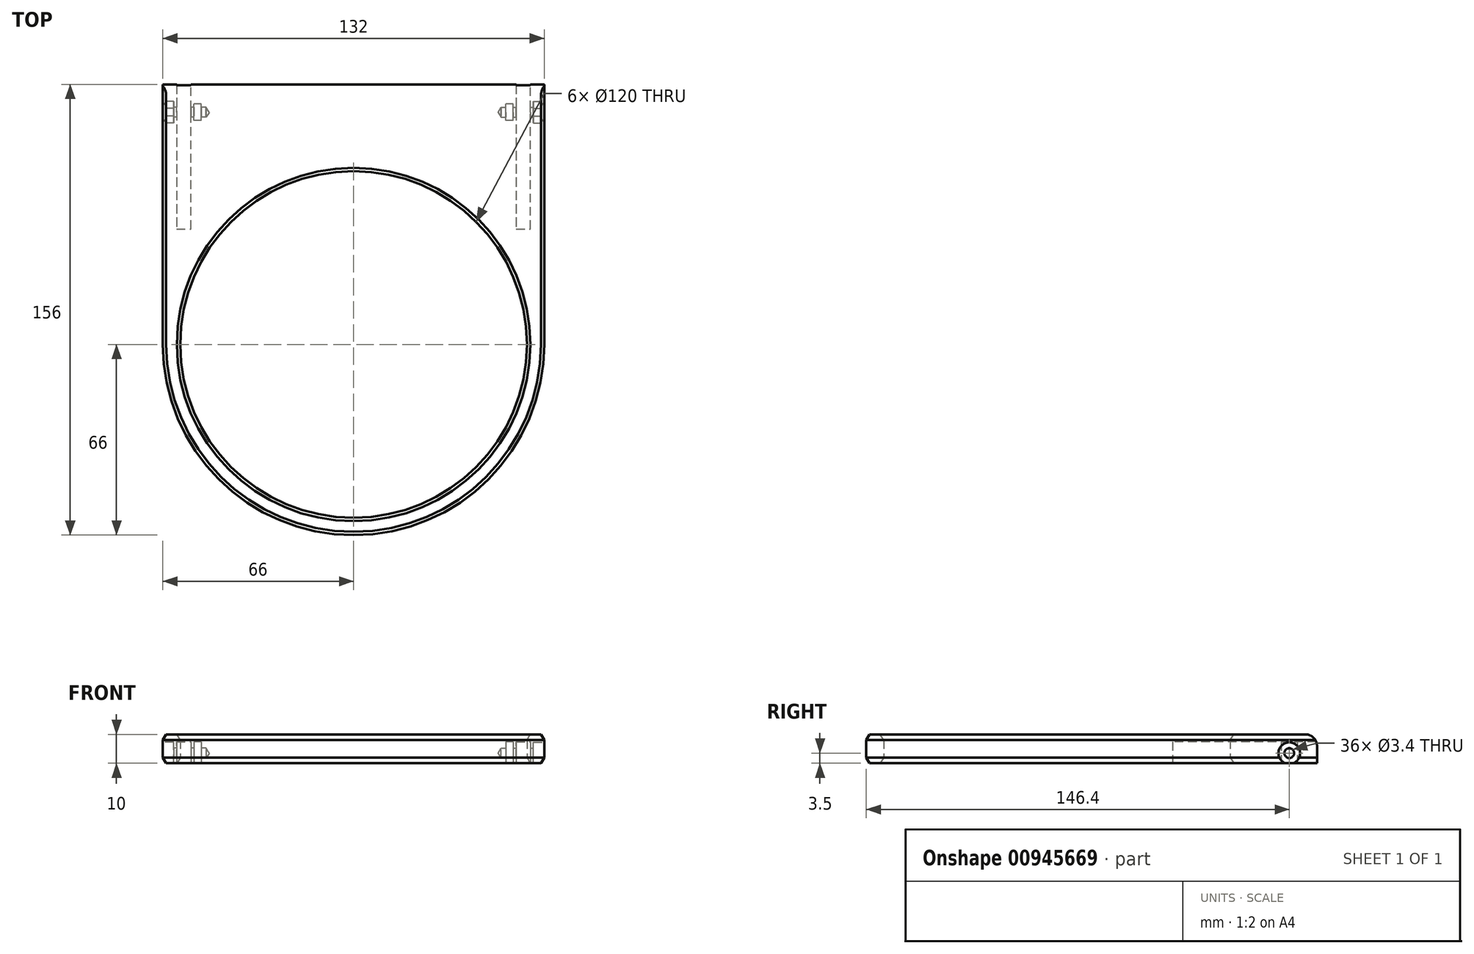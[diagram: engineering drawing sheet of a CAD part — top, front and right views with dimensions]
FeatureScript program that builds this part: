
annotation { "Feature Type Name" : "Feature", "Feature Type Description" : "" }
export const myFeature = defineFeature(function(context is Context, id is Id, definition is map)
    precondition{}
    {
        {
            var Q0;
            Q0=qCreatedBy(makeId("Top.planeOp"),FACE);
            var sketch = newSketch(context, id + "F0", { "sketchPlane" : qUnion([Q0])});
            skArc(sketch, "E0", {"start": v(-66, 0) * mm, "mid": v(0, -66) * mm, "end": v(66, 0) * mm});
            skLineSegment(sketch, "E1", {"start": v(-66, 0) * mm, "end": v(-66, 90) * mm});
            skLineSegment(sketch, "E2", {"start": v(-66, 90) * mm, "end": v(66, 90) * mm});
            skLineSegment(sketch, "E3", {"start": v(66, 90) * mm, "end": v(66, 0) * mm});
            skCircle(sketch, "E4", {"center": v(0, 0) * mm, "radius": 60 * mm});
            skSolve(sketch);
        }
        {
            var Q0;
            Q0=makeQuery(id+"F0.imprint","IMPRINT",FACE,{"disambiguationData":[TD([[makeQuery(id+"F0.imprint","IMPRINT",EDGE,{"derivedFrom":sQuery(id+"F0.wireOp",EDGE,"E0")}),1.0]])]});
            extrude(context, id + "F1", {"entities" : qUnion([Q0]), "depth" : 10 * mm, "offsetDistance" : 25 * mm});
        }
        {
            var Q0;
            Q0=makeQuery(id+"F1.opExtrude","CAP_EDGE",EDGE,{"disambiguationData":[OSD([sQuery(id+"F0.wireOp",EDGE,"E0")])],"isStart":true});
            var Q1;
            Q1=makeQuery(id+"F1.opExtrude","CAP_EDGE",EDGE,{"disambiguationData":[OSD([sQuery(id+"F0.wireOp",EDGE,"E0")])],"isStart":false});
            var Q2;
            Q2=makeQuery(id+"F1.opExtrude","CAP_EDGE",EDGE,{"disambiguationData":[OSD([sQuery(id+"F0.wireOp",EDGE,"E4")])],"isStart":false});
            var Q3;
            Q3=makeQuery(id+"F1.opExtrude","CAP_EDGE",EDGE,{"disambiguationData":[OSD([sQuery(id+"F0.wireOp",EDGE,"E4")])],"isStart":true});
            chamfer(context, id + "F2", {"entities" : qUnion([Q0, Q1, Q2, Q3]), "chamferType" : ChamferType.OFFSET_ANGLE, "width" : 2 * mm, "oppositeDirection" : false, "angle" : 30 * degree, "tangentPropagation" : true});
        }
        {
            var Q0;
            Q0=makeQuery(id+"F1.opExtrude","CAP_EDGE",EDGE,{"disambiguationData":[OSD([sQuery(id+"F0.wireOp",EDGE,"E2")])],"isStart":false});
            fillet(context, id + "F3", {"entities" : qUnion([Q0]), "radius" : 4 * mm, "tangentPropagation" : true, "allowEdgeOverflow" : false});
        }
        {
            var Q0;
            Q0=makeQuery(id+"F1.opExtrude","CAP_FACE",FACE,{"disambiguationData":[OSD([sQuery(id+"F0.wireOp",EDGE,"E0"),sQuery(id+"F0.wireOp",EDGE,"E1"),sQuery(id+"F0.wireOp",EDGE,"E2"),sQuery(id+"F0.wireOp",EDGE,"E3"),sQuery(id+"F0.wireOp",EDGE,"E4")])],"isStart":true});
            var sketch = newSketch(context, id + "F4", { "sketchPlane" : qUnion([Q0])});
            skLineSegment(sketch, "E5", {"start": v(-61.25, -90) * mm, "end": v(-61.25, -40) * mm});
            skLineSegment(sketch, "E6", {"start": v(-61.25, -40) * mm, "end": v(-56.25, -40) * mm});
            skLineSegment(sketch, "E7", {"start": v(-56.25, -40) * mm, "end": v(-56.25, -90) * mm});
            skLineSegment(sketch, "E8", {"start": v(56.25, -90) * mm, "end": v(56.25, -40) * mm});
            skLineSegment(sketch, "E9", {"start": v(56.25, -40) * mm, "end": v(61.25, -40) * mm});
            skLineSegment(sketch, "E10", {"start": v(61.25, -40) * mm, "end": v(61.25, -90) * mm});
            skLineSegment(sketch, "E11.bottom", {"start": v(-52.65, -77.55) * mm, "end": v(-55.25, -77.55) * mm});
            skLineSegment(sketch, "E11.top", {"start": v(-52.65, -83.25) * mm, "end": v(-55.25, -83.25) * mm});
            skLineSegment(sketch, "E11.left", {"start": v(-52.65, -77.55) * mm, "end": v(-52.65, -83.25) * mm});
            skLineSegment(sketch, "E11.right", {"start": v(-55.25, -77.55) * mm, "end": v(-55.25, -83.25) * mm});
            skPoint(sketch, "E11.middle", {"position": v(-53.95, -80.4) * mm});
            skLineSegment(sketch, "E12.bottom", {"start": v(55.25, -77.55) * mm, "end": v(52.65, -77.55) * mm});
            skLineSegment(sketch, "E12.top", {"start": v(55.25, -83.25) * mm, "end": v(52.65, -83.25) * mm});
            skLineSegment(sketch, "E12.left", {"start": v(55.25, -77.55) * mm, "end": v(55.25, -83.25) * mm});
            skLineSegment(sketch, "E12.right", {"start": v(52.65, -77.55) * mm, "end": v(52.65, -83.25) * mm});
            skPoint(sketch, "E12.middle", {"position": v(53.95, -80.4) * mm});
            skSolve(sketch);
        }
        {
            var Q0;
            {var subQ0=sQuery(id+"F4.wireOp",EDGE,"E8");Q0=makeQuery(id+"F4.imprint","IMPRINT",FACE,{"disambiguationData":[TD([[makeQuery(id+"F4.imprint","IMPRINT",EDGE,{"derivedFrom":subQ0}),-1.0]])]});}
            var Q1;
            {var subQ0=sQuery(id+"F4.wireOp",EDGE,"E5");Q1=makeQuery(id+"F4.imprint","IMPRINT",FACE,{"disambiguationData":[TD([[makeQuery(id+"F4.imprint","IMPRINT",EDGE,{"derivedFrom":subQ0}),-1.0]])]});}
            var Q2;
            Q2=makeQuery(id+"F4.imprint","IMPRINT",FACE,{"disambiguationData":[TD([[makeQuery(id+"F4.imprint","IMPRINT",EDGE,{"derivedFrom":sQuery(id+"F4.wireOp",EDGE,"E11.bottom")}),1.0]])]});
            var Q3;
            Q3=makeQuery(id+"F4.imprint","IMPRINT",FACE,{"disambiguationData":[TD([[makeQuery(id+"F4.imprint","IMPRINT",EDGE,{"derivedFrom":sQuery(id+"F4.wireOp",EDGE,"E12.bottom")}),1.0]])]});
            extrude(context, id + "F5", {"entities" : qUnion([Q0, Q1, Q2, Q3]), "operationType" : NewBodyOperationType.REMOVE, "oppositeDirection" : true, "depth" : 7.4 * mm, "offsetDistance" : 25 * mm});
        }
        {
            var Q0;
            Q0=makeQuery(id+"F1.opExtrude","SWEPT_FACE",FACE,{"disambiguationData":[OSD([sQuery(id+"F0.wireOp",EDGE,"E1")])]});
            var sketch = newSketch(context, id + "F6", { "sketchPlane" : qUnion([Q0])});
            skPoint(sketch, "E13", {"position": v(-80.4, 3.5) * mm});
            skSolve(sketch);
        }
        {
            var Q0;
            Q0=makeQuery(id+"F1.opExtrude","SWEPT_FACE",FACE,{"disambiguationData":[OSD([sQuery(id+"F0.wireOp",EDGE,"E3")])]});
            var sketch = newSketch(context, id + "F7", { "sketchPlane" : qUnion([Q0])});
            skPoint(sketch, "E14", {"position": v(80.4, 3.5) * mm});
            skSolve(sketch);
        }
        {
            var Q0;
            Q0=sQuery(id+"F6.wireOp",VERTEX,"E13");
            var Q1;
            Q1=sQuery(id+"F7.wireOp",VERTEX,"E14");
            var Q2;
            Q2=makeQuery(id+"F1.opExtrude","SWEPT_BODY",BODY,{"disambiguationData":[OSD([sQuery(id+"F0.wireOp",EDGE,"E0"),sQuery(id+"F0.wireOp",EDGE,"E1"),sQuery(id+"F0.wireOp",EDGE,"E2"),sQuery(id+"F0.wireOp",EDGE,"E3"),sQuery(id+"F0.wireOp",EDGE,"E4")])]});
            hole(context, id + "F8", {"style" : HoleStyle.C_BORE, "endStyle" : HoleEndStyle.BLIND, "holeDiameter" : 3.4 * mm, "cBoreDiameter" : 7.5 * mm, "cBoreDepth" : 3.75 * mm, "majorDiameter" : 5 * mm, "holeDepth" : 15 * mm, "isTappedThrough" : true, "tappedDepth" : 12 * mm, "tapClearance" : 3, "locations" : qUnion([Q0, Q1]), "scope" : qUnion([Q2])});
        }
    });
